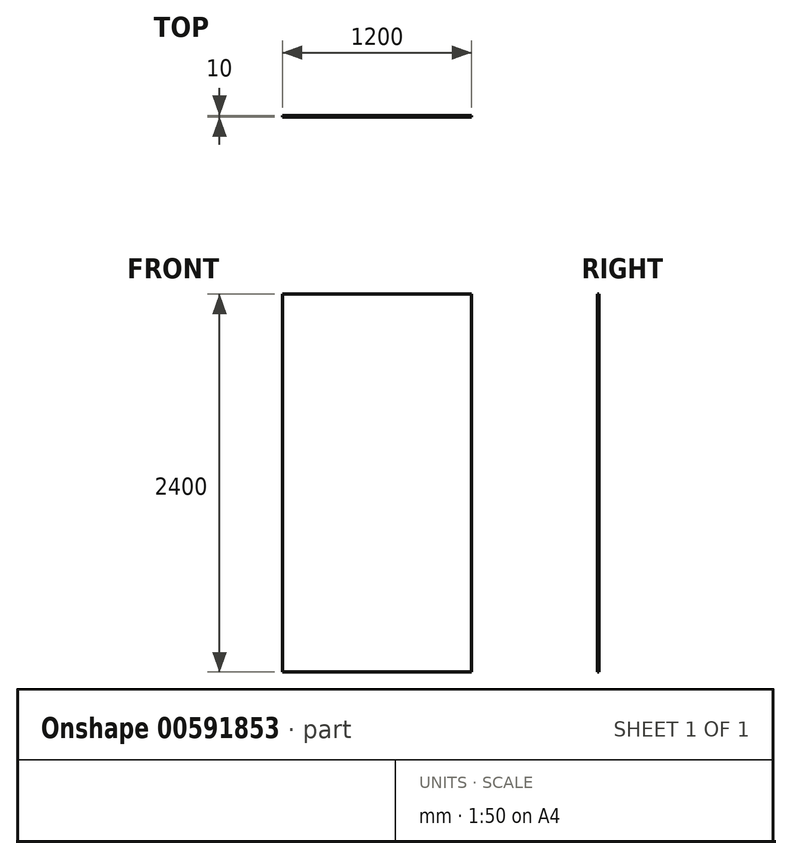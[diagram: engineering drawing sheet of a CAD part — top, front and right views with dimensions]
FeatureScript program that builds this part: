
annotation { "Feature Type Name" : "Feature", "Feature Type Description" : "" }
export const myFeature = defineFeature(function(context is Context, id is Id, definition is map)
    precondition{}
    {
        {
            var Q0;
            Q0=qCreatedBy(makeId("Front.planeOp"),FACE);
            var sketch = newSketch(context, id + "F0", { "sketchPlane" : qUnion([Q0])});
            skLineSegment(sketch, "E0.bottom", {"start": v(0, 0) * mm, "end": v(1200, 0) * mm});
            skLineSegment(sketch, "E0.top", {"start": v(0, 2400) * mm, "end": v(1200, 2400) * mm});
            skLineSegment(sketch, "E0.left", {"start": v(0, 0) * mm, "end": v(0, 2400) * mm});
            skLineSegment(sketch, "E0.right", {"start": v(1200, 0) * mm, "end": v(1200, 2400) * mm});
            skSolve(sketch);
        }
        {
            var Q0;
            Q0=makeQuery(id+"F0.imprint","IMPRINT",FACE,{"disambiguationData":[TD([[makeQuery(id+"F0.imprint","IMPRINT",EDGE,{"derivedFrom":sQuery(id+"F0.wireOp",EDGE,"E0.bottom")}),1.0]])]});
            extrude(context, id + "F1", {"entities" : qUnion([Q0]), "depth" : 10 * mm, "offsetDistance" : 25 * mm});
        }
    });
